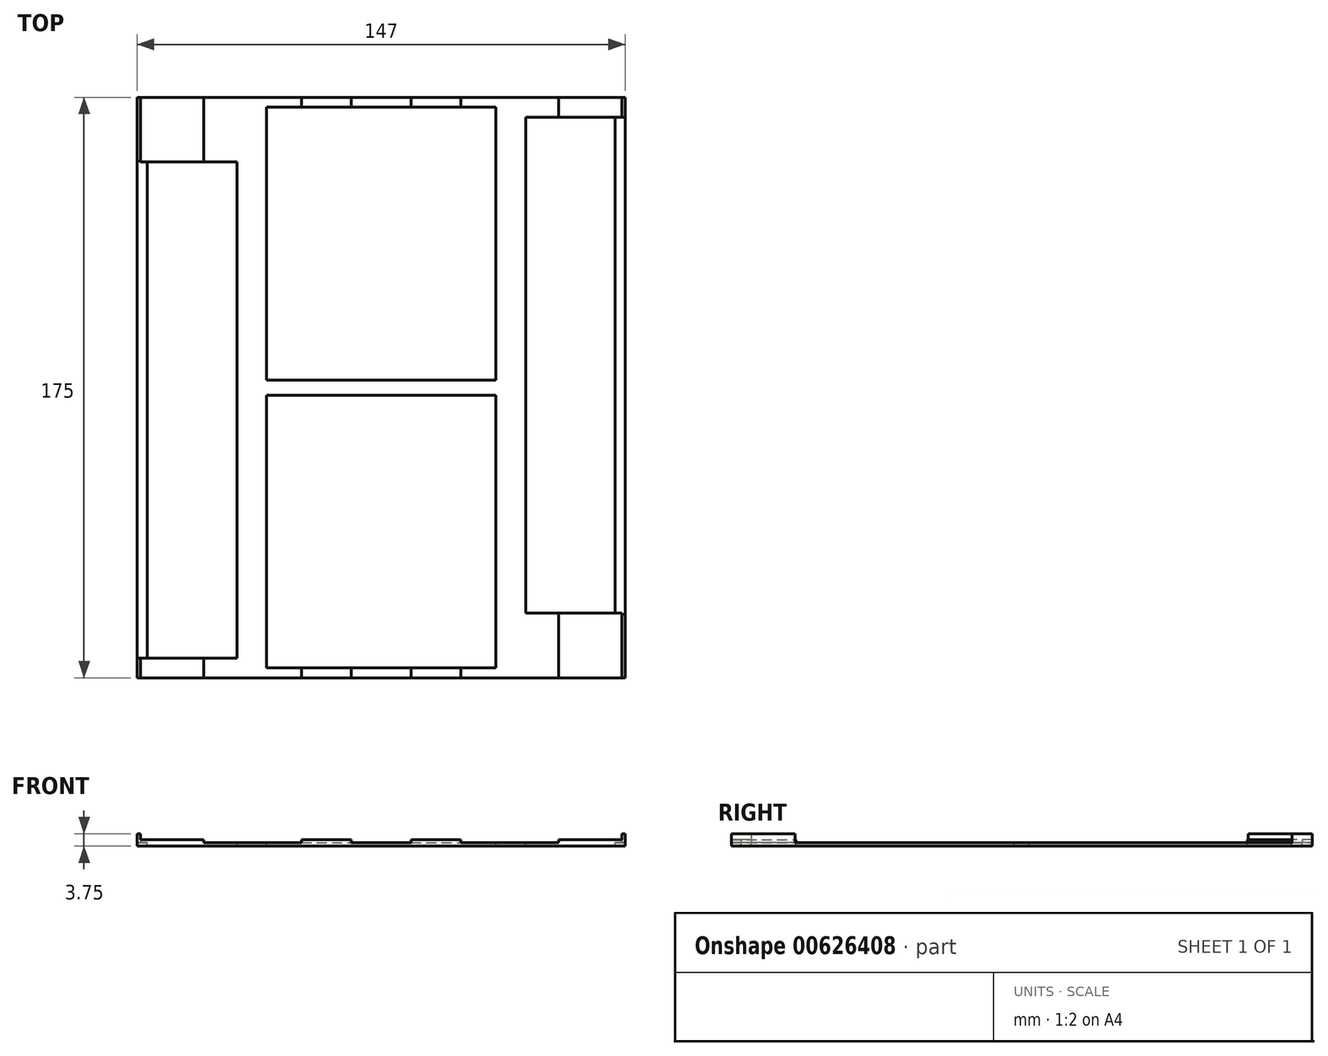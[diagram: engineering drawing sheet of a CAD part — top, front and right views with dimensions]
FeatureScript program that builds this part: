
annotation { "Feature Type Name" : "Feature", "Feature Type Description" : "" }
export const myFeature = defineFeature(function(context is Context, id is Id, definition is map)
    precondition{}
    {
        {
            var Q0;
            Q0=qCreatedBy(makeId("Top.planeOp"),FACE);
            var sketch = newSketch(context, id + "F0", { "sketchPlane" : qUnion([Q0])});
            skLineSegment(sketch, "E0.bottom", {"start": v(0, 0) * mm, "end": v(156, 0) * mm});
            skLineSegment(sketch, "E0.top", {"start": v(0, 175) * mm, "end": v(156, 175) * mm});
            skLineSegment(sketch, "E0.left", {"start": v(0, 0) * mm, "end": v(0, 175) * mm});
            skLineSegment(sketch, "E0.right", {"start": v(156, 0) * mm, "end": v(156, 175) * mm});
            skSolve(sketch);
        }
        {
            var Q0;
            Q0=makeQuery(id+"F0.imprint","IMPRINT",FACE,{"disambiguationData":[TD([[makeQuery(id+"F0.imprint","IMPRINT",EDGE,{"derivedFrom":sQuery(id+"F0.wireOp",EDGE,"E0.bottom")}),1.0]])]});
            extrude(context, id + "F1", {"entities" : qUnion([Q0]), "depth" : 1 * mm, "offsetDistance" : 25 * mm});
        }
        {
            var Q0;
            Q0=makeQuery(id+"F1.opExtrude","CAP_FACE",FACE,{"disambiguationData":[OSD([sQuery(id+"F0.wireOp",EDGE,"E0.bottom"),sQuery(id+"F0.wireOp",EDGE,"E0.top"),sQuery(id+"F0.wireOp",EDGE,"E0.left"),sQuery(id+"F0.wireOp",EDGE,"E0.right")])],"isStart":false});
            var sketch = newSketch(context, id + "F2", { "sketchPlane" : qUnion([Q0])});
            skLineSegment(sketch, "E1.bottom", {"start": v(0, 175) * mm, "end": v(4.5, 175) * mm});
            skLineSegment(sketch, "E1.top", {"start": v(0, 0) * mm, "end": v(4.5, 0) * mm});
            skLineSegment(sketch, "E1.left", {"start": v(0, 175) * mm, "end": v(0, 0) * mm});
            skLineSegment(sketch, "E1.right", {"start": v(4.5, 175) * mm, "end": v(4.5, 0) * mm});
            skLineSegment(sketch, "E2.bottom", {"start": v(156, 175) * mm, "end": v(151.5, 175) * mm});
            skLineSegment(sketch, "E2.top", {"start": v(156, 0) * mm, "end": v(151.5, 0) * mm});
            skLineSegment(sketch, "E2.left", {"start": v(156, 175) * mm, "end": v(156, 0) * mm});
            skLineSegment(sketch, "E2.right", {"start": v(151.5, 175) * mm, "end": v(151.5, 0) * mm});
            skLineSegment(sketch, "E3.bottom", {"start": v(7.5, 155.5) * mm, "end": v(34.5, 155.5) * mm});
            skLineSegment(sketch, "E3.top", {"start": v(7.5, 6) * mm, "end": v(34.5, 6) * mm});
            skLineSegment(sketch, "E3.left", {"start": v(7.5, 155.5) * mm, "end": v(7.5, 6) * mm});
            skLineSegment(sketch, "E3.right", {"start": v(34.5, 155.5) * mm, "end": v(34.5, 6) * mm});
            skLineSegment(sketch, "E4.bottom", {"start": v(148.5, 19.5) * mm, "end": v(121.5, 19.5) * mm});
            skLineSegment(sketch, "E4.top", {"start": v(148.5, 169) * mm, "end": v(121.5, 169) * mm});
            skLineSegment(sketch, "E4.left", {"start": v(148.5, 19.5) * mm, "end": v(148.5, 169) * mm});
            skLineSegment(sketch, "E4.right", {"start": v(121.5, 19.5) * mm, "end": v(121.5, 169) * mm});
            skLineSegment(sketch, "E5.bottom", {"start": v(43.5, 172) * mm, "end": v(112.5, 172) * mm});
            skLineSegment(sketch, "E5.top", {"start": v(43.5, 89.75) * mm, "end": v(112.5, 89.75) * mm});
            skLineSegment(sketch, "E5.left", {"start": v(43.5, 172) * mm, "end": v(43.5, 89.75) * mm});
            skLineSegment(sketch, "E5.right", {"start": v(112.5, 172) * mm, "end": v(112.5, 89.75) * mm});
            skLineSegment(sketch, "E6.bottom", {"start": v(43.5, 85.25) * mm, "end": v(112.5, 85.25) * mm});
            skLineSegment(sketch, "E6.top", {"start": v(43.5, 3) * mm, "end": v(112.5, 3) * mm});
            skLineSegment(sketch, "E6.left", {"start": v(43.5, 85.25) * mm, "end": v(43.5, 3) * mm});
            skLineSegment(sketch, "E6.right", {"start": v(112.5, 85.25) * mm, "end": v(112.5, 3) * mm});
            skSolve(sketch);
        }
        {
            var Q0;
            Q0=makeQuery(id+"F2.imprint","IMPRINT",FACE,{"disambiguationData":[TD([[makeQuery(id+"F2.imprint","IMPRINT",EDGE,{"derivedFrom":sQuery(id+"F2.wireOp",EDGE,"E1.bottom")}),-1.0]])]});
            var Q1;
            Q1=makeQuery(id+"F2.imprint","IMPRINT",FACE,{"disambiguationData":[TD([[makeQuery(id+"F2.imprint","IMPRINT",EDGE,{"derivedFrom":sQuery(id+"F2.wireOp",EDGE,"E3.bottom")}),-1.0]])]});
            var Q2;
            Q2=makeQuery(id+"F2.imprint","IMPRINT",FACE,{"disambiguationData":[TD([[makeQuery(id+"F2.imprint","IMPRINT",EDGE,{"derivedFrom":sQuery(id+"F2.wireOp",EDGE,"E5.bottom")}),-1.0]])]});
            var Q3;
            Q3=makeQuery(id+"F2.imprint","IMPRINT",FACE,{"disambiguationData":[TD([[makeQuery(id+"F2.imprint","IMPRINT",EDGE,{"derivedFrom":sQuery(id+"F2.wireOp",EDGE,"E6.bottom")}),-1.0]])]});
            var Q4;
            Q4=makeQuery(id+"F2.imprint","IMPRINT",FACE,{"disambiguationData":[TD([[makeQuery(id+"F2.imprint","IMPRINT",EDGE,{"derivedFrom":sQuery(id+"F2.wireOp",EDGE,"E4.bottom")}),-1.0]])]});
            var Q5;
            Q5=makeQuery(id+"F2.imprint","IMPRINT",FACE,{"disambiguationData":[TD([[makeQuery(id+"F2.imprint","IMPRINT",EDGE,{"derivedFrom":sQuery(id+"F2.wireOp",EDGE,"E2.bottom")}),-1.0]])]});
            extrude(context, id + "F3", {"entities" : qUnion([Q0, Q1, Q2, Q3, Q4, Q5]), "operationType" : NewBodyOperationType.REMOVE, "endBound" : BoundingType.THROUGH_ALL, "oppositeDirection" : true, "depth" : 25 * mm, "offsetDistance" : 25 * mm});
        }
        {
            var Q0;
            Q0=makeQuery(id+"F1.opExtrude","CAP_FACE",FACE,{"disambiguationData":[OSD([sQuery(id+"F0.wireOp",EDGE,"E0.bottom"),sQuery(id+"F0.wireOp",EDGE,"E0.top"),sQuery(id+"F0.wireOp",EDGE,"E0.left"),sQuery(id+"F0.wireOp",EDGE,"E0.right")])],"isStart":false});
            var sketch = newSketch(context, id + "F4", { "sketchPlane" : qUnion([Q0])});
            skLineSegment(sketch, "E7.bottom", {"start": v(54, 175) * mm, "end": v(69, 175) * mm});
            skLineSegment(sketch, "E7.top", {"start": v(54, 172) * mm, "end": v(69, 172) * mm});
            skLineSegment(sketch, "E7.left", {"start": v(54, 175) * mm, "end": v(54, 172) * mm});
            skLineSegment(sketch, "E7.right", {"start": v(69, 175) * mm, "end": v(69, 172) * mm});
            skLineSegment(sketch, "E8.bottom", {"start": v(87, 175) * mm, "end": v(102, 175) * mm});
            skLineSegment(sketch, "E8.top", {"start": v(87, 172) * mm, "end": v(102, 172) * mm});
            skLineSegment(sketch, "E8.left", {"start": v(87, 175) * mm, "end": v(87, 172) * mm});
            skLineSegment(sketch, "E8.right", {"start": v(102, 175) * mm, "end": v(102, 172) * mm});
            skLineSegment(sketch, "E9.bottom", {"start": v(24.5, 175) * mm, "end": v(5.5, 175) * mm});
            skLineSegment(sketch, "E9.top", {"start": v(24.5, 155.5) * mm, "end": v(5.5, 155.5) * mm});
            skLineSegment(sketch, "E9.left", {"start": v(24.5, 175) * mm, "end": v(24.5, 155.5) * mm});
            skLineSegment(sketch, "E9.right", {"start": v(5.5, 175) * mm, "end": v(5.5, 155.5) * mm});
            skLineSegment(sketch, "E10.bottom", {"start": v(54, 3) * mm, "end": v(69, 3) * mm});
            skLineSegment(sketch, "E10.top", {"start": v(54, 0) * mm, "end": v(69, 0) * mm});
            skLineSegment(sketch, "E10.left", {"start": v(54, 3) * mm, "end": v(54, 0) * mm});
            skLineSegment(sketch, "E10.right", {"start": v(69, 3) * mm, "end": v(69, 0) * mm});
            skLineSegment(sketch, "E11.bottom", {"start": v(87, 3) * mm, "end": v(102, 3) * mm});
            skLineSegment(sketch, "E11.top", {"start": v(87, 0) * mm, "end": v(102, 0) * mm});
            skLineSegment(sketch, "E11.left", {"start": v(87, 3) * mm, "end": v(87, 0) * mm});
            skLineSegment(sketch, "E11.right", {"start": v(102, 3) * mm, "end": v(102, 0) * mm});
            skLineSegment(sketch, "E12.bottom", {"start": v(131.5, 0) * mm, "end": v(150.5, 0) * mm});
            skLineSegment(sketch, "E12.top", {"start": v(131.5, 19.5) * mm, "end": v(150.5, 19.5) * mm});
            skLineSegment(sketch, "E12.left", {"start": v(131.5, 0) * mm, "end": v(131.5, 19.5) * mm});
            skLineSegment(sketch, "E12.right", {"start": v(150.5, 0) * mm, "end": v(150.5, 19.5) * mm});
            skSolve(sketch);
        }
        {
            var Q0;
            Q0=makeQuery(id+"F4.imprint","IMPRINT",FACE,{"disambiguationData":[TD([[makeQuery(id+"F4.imprint","IMPRINT",EDGE,{"derivedFrom":sQuery(id+"F4.wireOp",EDGE,"E9.bottom")}),-1.0]])]});
            var Q1;
            Q1=makeQuery(id+"F4.imprint","IMPRINT",FACE,{"disambiguationData":[TD([[makeQuery(id+"F4.imprint","IMPRINT",EDGE,{"derivedFrom":sQuery(id+"F4.wireOp",EDGE,"E7.bottom")}),-1.0]])]});
            var Q2;
            Q2=makeQuery(id+"F4.imprint","IMPRINT",FACE,{"disambiguationData":[TD([[makeQuery(id+"F4.imprint","IMPRINT",EDGE,{"derivedFrom":sQuery(id+"F4.wireOp",EDGE,"E8.bottom")}),-1.0]])]});
            var Q3;
            Q3=makeQuery(id+"F4.imprint","IMPRINT",FACE,{"disambiguationData":[TD([[makeQuery(id+"F4.imprint","IMPRINT",EDGE,{"derivedFrom":sQuery(id+"F4.wireOp",EDGE,"E12.bottom")}),1.0]])]});
            var Q4;
            Q4=makeQuery(id+"F4.imprint","IMPRINT",FACE,{"disambiguationData":[TD([[makeQuery(id+"F4.imprint","IMPRINT",EDGE,{"derivedFrom":sQuery(id+"F4.wireOp",EDGE,"E11.bottom")}),-1.0]])]});
            var Q5;
            Q5=makeQuery(id+"F4.imprint","IMPRINT",FACE,{"disambiguationData":[TD([[makeQuery(id+"F4.imprint","IMPRINT",EDGE,{"derivedFrom":sQuery(id+"F4.wireOp",EDGE,"E10.bottom")}),-1.0]])]});
            extrude(context, id + "F5", {"entities" : qUnion([Q0, Q1, Q2, Q3, Q4, Q5]), "operationType" : NewBodyOperationType.ADD, "depth" : 1 * mm, "offsetDistance" : 25 * mm});
        }
        {
            var Q0;
            {var subQ0=sQuery(id+"F0.wireOp",EDGE,"E0.top");var subQ1=sQuery(id+"F0.wireOp",EDGE,"E0.bottom");Q0=makeQuery(id+"F5.boolean.opBoolean","SPLIT",FACE,{"disambiguationData":[TD([makeQuery(id+"F3.boolean.opBoolean","COPY",FACE,{"derivedFrom":makeQuery(id+"F3.opExtrude","SWEPT_FACE",FACE,{"disambiguationData":[OSD([sQuery(id+"F2.wireOp",EDGE,"E1.right")])]})})])],"derivedFrom":makeQuery(id+"F1.opExtrude","CAP_FACE",FACE,{"disambiguationData":[OSD([subQ1,subQ0,sQuery(id+"F0.wireOp",EDGE,"E0.left"),sQuery(id+"F0.wireOp",EDGE,"E0.right")])],"isStart":false})});}
            var sketch = newSketch(context, id + "F6", { "sketchPlane" : qUnion([Q0])});
            skLineSegment(sketch, "E13.bottom", {"start": v(150.5, 0) * mm, "end": v(151.5, 0) * mm});
            skLineSegment(sketch, "E13.top", {"start": v(150.5, 19.18) * mm, "end": v(151.5, 19.18) * mm});
            skLineSegment(sketch, "E13.left", {"start": v(150.5, 0) * mm, "end": v(150.5, 19.18) * mm});
            skLineSegment(sketch, "E13.right", {"start": v(151.5, 0) * mm, "end": v(151.5, 19.18) * mm});
            skLineSegment(sketch, "E14.bottom", {"start": v(5.5, 175) * mm, "end": v(4.5, 175) * mm});
            skLineSegment(sketch, "E14.top", {"start": v(5.5, 155.74) * mm, "end": v(4.5, 155.74) * mm});
            skLineSegment(sketch, "E14.left", {"start": v(5.5, 175) * mm, "end": v(5.5, 155.74) * mm});
            skLineSegment(sketch, "E14.right", {"start": v(4.5, 175) * mm, "end": v(4.5, 155.74) * mm});
            skSolve(sketch);
        }
        {
            var Q0;
            Q0=makeQuery(id+"F6.imprint","IMPRINT",FACE,{"disambiguationData":[TD([[makeQuery(id+"F6.imprint","IMPRINT",EDGE,{"derivedFrom":sQuery(id+"F6.wireOp",EDGE,"E13.bottom")}),1.0]])]});
            var Q1;
            Q1=makeQuery(id+"F6.imprint","IMPRINT",FACE,{"disambiguationData":[TD([[makeQuery(id+"F6.imprint","IMPRINT",EDGE,{"derivedFrom":sQuery(id+"F6.wireOp",EDGE,"E14.bottom")}),-1.0]])]});
            extrude(context, id + "F7", {"entities" : qUnion([Q0, Q1]), "operationType" : NewBodyOperationType.ADD, "depth" : 2.75 * mm, "offsetDistance" : 25 * mm});
        }
        {
            var Q0;
            {var subQ0=sQuery(id+"F0.wireOp",EDGE,"E0.top");var subQ1=sQuery(id+"F0.wireOp",EDGE,"E0.bottom");Q0=makeQuery(id+"F5.boolean.opBoolean","SPLIT",FACE,{"disambiguationData":[TD([makeQuery(id+"F3.boolean.opBoolean","COPY",FACE,{"derivedFrom":makeQuery(id+"F3.opExtrude","SWEPT_FACE",FACE,{"disambiguationData":[OSD([sQuery(id+"F2.wireOp",EDGE,"E1.right")])]})})])],"derivedFrom":makeQuery(id+"F1.opExtrude","CAP_FACE",FACE,{"disambiguationData":[OSD([subQ1,subQ0,sQuery(id+"F0.wireOp",EDGE,"E0.left"),sQuery(id+"F0.wireOp",EDGE,"E0.right")])],"isStart":false})});}
            var sketch = newSketch(context, id + "F8", { "sketchPlane" : qUnion([Q0])});
            skLineSegment(sketch, "E15.bottom", {"start": v(131.5, 169) * mm, "end": v(150.5, 169) * mm});
            skLineSegment(sketch, "E15.top", {"start": v(131.5, 175) * mm, "end": v(150.5, 175) * mm});
            skLineSegment(sketch, "E15.left", {"start": v(131.5, 169) * mm, "end": v(131.5, 175) * mm});
            skLineSegment(sketch, "E15.right", {"start": v(150.5, 169) * mm, "end": v(150.5, 175) * mm});
            skLineSegment(sketch, "E16.bottom", {"start": v(24.5, 6) * mm, "end": v(5.5, 6) * mm});
            skLineSegment(sketch, "E16.top", {"start": v(24.5, 0) * mm, "end": v(5.5, 0) * mm});
            skLineSegment(sketch, "E16.left", {"start": v(24.5, 6) * mm, "end": v(24.5, 0) * mm});
            skLineSegment(sketch, "E16.right", {"start": v(5.5, 6) * mm, "end": v(5.5, 0) * mm});
            skSolve(sketch);
        }
        {
            var Q0;
            Q0=makeQuery(id+"F8.imprint","IMPRINT",FACE,{"disambiguationData":[TD([[makeQuery(id+"F8.imprint","IMPRINT",EDGE,{"derivedFrom":sQuery(id+"F8.wireOp",EDGE,"E16.top")}),1.0]])]});
            var Q1;
            Q1=makeQuery(id+"F8.imprint","IMPRINT",FACE,{"disambiguationData":[TD([[makeQuery(id+"F8.imprint","IMPRINT",EDGE,{"derivedFrom":sQuery(id+"F8.wireOp",EDGE,"E15.top")}),-1.0]])]});
            extrude(context, id + "F9", {"entities" : qUnion([Q0, Q1]), "operationType" : NewBodyOperationType.ADD, "depth" : 1 * mm, "offsetDistance" : 25 * mm});
        }
        {
            var Q0;
            {var subQ3=sQuery(id+"F0.wireOp",EDGE,"E0.top");var subQ7=makeQuery(id+"F3.boolean.opBoolean","COPY",FACE,{"derivedFrom":makeQuery(id+"F3.opExtrude","SWEPT_FACE",FACE,{"disambiguationData":[OSD([sQuery(id+"F2.wireOp",EDGE,"E2.right")])]})});var subQ11=sQuery(id+"F0.wireOp",EDGE,"E0.bottom");Q0=makeQuery(id+"F9.boolean.opBoolean","SPLIT",FACE,{"disambiguationData":[TD([subQ7])],"derivedFrom":makeQuery(id+"F5.boolean.opBoolean","SPLIT",FACE,{"disambiguationData":[TD([makeQuery(id+"F3.boolean.opBoolean","COPY",FACE,{"derivedFrom":makeQuery(id+"F3.opExtrude","SWEPT_FACE",FACE,{"disambiguationData":[OSD([sQuery(id+"F2.wireOp",EDGE,"E1.right")])]})})])],"derivedFrom":makeQuery(id+"F1.opExtrude","CAP_FACE",FACE,{"disambiguationData":[OSD([subQ11,subQ3,sQuery(id+"F0.wireOp",EDGE,"E0.left"),sQuery(id+"F0.wireOp",EDGE,"E0.right")])],"isStart":false})})});}
            var sketch = newSketch(context, id + "F10", { "sketchPlane" : qUnion([Q0])});
            skLineSegment(sketch, "E17.bottom", {"start": v(151.5, 175) * mm, "end": v(150.5, 175) * mm});
            skLineSegment(sketch, "E17.top", {"start": v(151.5, 169) * mm, "end": v(150.5, 169) * mm});
            skLineSegment(sketch, "E17.left", {"start": v(151.5, 175) * mm, "end": v(151.5, 169) * mm});
            skLineSegment(sketch, "E17.right", {"start": v(150.5, 175) * mm, "end": v(150.5, 169) * mm});
            skSolve(sketch);
        }
        {
            var Q0;
            Q0=makeQuery(id+"F10.imprint","IMPRINT",FACE,{"disambiguationData":[TD([[makeQuery(id+"F10.imprint","IMPRINT",EDGE,{"derivedFrom":sQuery(id+"F10.wireOp",EDGE,"E17.bottom")}),-1.0]])]});
            extrude(context, id + "F11", {"entities" : qUnion([Q0]), "operationType" : NewBodyOperationType.ADD, "depth" : 2.75 * mm, "offsetDistance" : 25 * mm});
        }
        {
            var Q0;
            {var subQ5=sQuery(id+"F0.wireOp",EDGE,"E0.bottom");var subQ9=makeQuery(id+"F3.boolean.opBoolean","COPY",FACE,{"derivedFrom":makeQuery(id+"F3.opExtrude","SWEPT_FACE",FACE,{"disambiguationData":[OSD([sQuery(id+"F2.wireOp",EDGE,"E1.right")])]})});var subQ11=sQuery(id+"F0.wireOp",EDGE,"E0.top");Q0=makeQuery(id+"F9.boolean.opBoolean","SPLIT",FACE,{"disambiguationData":[TD([subQ9])],"derivedFrom":makeQuery(id+"F5.boolean.opBoolean","SPLIT",FACE,{"disambiguationData":[TD([subQ9])],"derivedFrom":makeQuery(id+"F1.opExtrude","CAP_FACE",FACE,{"disambiguationData":[OSD([subQ5,subQ11,sQuery(id+"F0.wireOp",EDGE,"E0.left"),sQuery(id+"F0.wireOp",EDGE,"E0.right")])],"isStart":false})})});}
            var sketch = newSketch(context, id + "F12", { "sketchPlane" : qUnion([Q0])});
            skLineSegment(sketch, "E18.bottom", {"start": v(5.5, 6) * mm, "end": v(4.5, 6) * mm});
            skLineSegment(sketch, "E18.top", {"start": v(5.5, 0) * mm, "end": v(4.5, 0) * mm});
            skLineSegment(sketch, "E18.left", {"start": v(5.5, 6) * mm, "end": v(5.5, 0) * mm});
            skLineSegment(sketch, "E18.right", {"start": v(4.5, 6) * mm, "end": v(4.5, 0) * mm});
            skSolve(sketch);
        }
        {
            var Q0;
            Q0=makeQuery(id+"F12.imprint","IMPRINT",FACE,{"disambiguationData":[TD([[makeQuery(id+"F12.imprint","IMPRINT",EDGE,{"derivedFrom":sQuery(id+"F12.wireOp",EDGE,"E18.bottom")}),1.0]])]});
            extrude(context, id + "F13", {"entities" : qUnion([Q0]), "operationType" : NewBodyOperationType.ADD, "depth" : 2.75 * mm, "offsetDistance" : 25 * mm});
        }
    });
